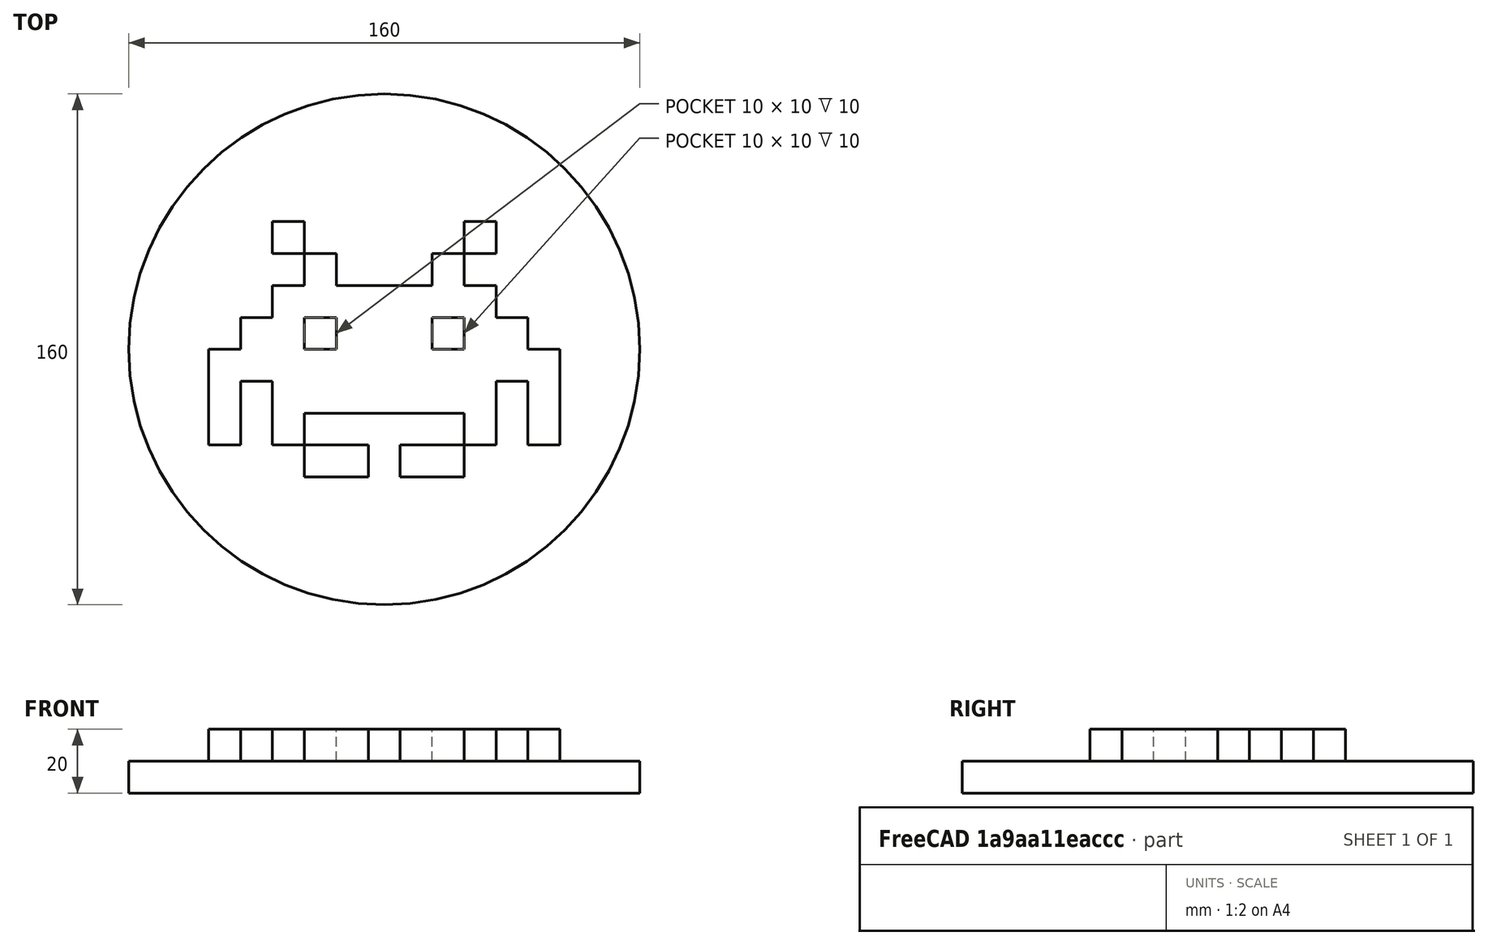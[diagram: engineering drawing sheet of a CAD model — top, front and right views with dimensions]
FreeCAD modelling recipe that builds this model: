
FCSTD DOCUMENT  (FreeCAD 0.17R13217 (Git))
Label: 02-1-moneda-space-invaders
License: All rights reserved
LicenseURL: http://en.wikipedia.org/wiki/All_rights_reserved
objects: Part::Box×18, Part::MultiFuse×2, Part::Cylinder×1
note: 21 computed .brp shape members not serialized (recipe doc carries the construction recipe); baked Part::Feature solids carry a one-line shape summary decoded from their .brp

FEATURE [Part::Box] Box  label="Cubo"
  AttacherType = Attacher::AttachEngine3D
  Height = 10
  Length = 10
  Width = 10
FEATURE [Part::Box] Box001  label="Cubo001"
  AttacherType = Attacher::AttachEngine3D
  Height = 10
  Length = 10
  Placement = pos=(10,-10,0) rot=(0,0,1;0rad)
  Width = 10
FEATURE [Part::Box] Box002  label="Cubo002"
  AttacherType = Attacher::AttachEngine3D
  Height = 10
  Length = 70
  Placement = pos=(0,-20,0) rot=(0,0,1;0rad)
  Width = 10
FEATURE [Part::Box] Box003  label="Cubo003"
  AttacherType = Attacher::AttachEngine3D
  Height = 10
  Length = 20
  Placement = pos=(-10,-30,0) rot=(0,0,1;0rad)
  Width = 10
FEATURE [Part::Box] Box004  label="Cubo004"
  AttacherType = Attacher::AttachEngine3D
  Height = 10
  Length = 10
  Placement = pos=(60,0,0) rot=(0,0,1;0rad)
  Width = 10
FEATURE [Part::Box] Box005  label="Cubo005"
  AttacherType = Attacher::AttachEngine3D
  Height = 10
  Length = 10
  Placement = pos=(50,-10,0) rot=(0,0,1;0rad)
  Width = 10
FEATURE [Part::Box] Box006  label="Cubo006"
  AttacherType = Attacher::AttachEngine3D
  Height = 10
  Length = 30
  Placement = pos=(20,-30,0) rot=(0,0,1;0rad)
  Width = 10
FEATURE [Part::Box] Box007  label="Cubo007"
  AttacherType = Attacher::AttachEngine3D
  Height = 10
  Length = 20
  Placement = pos=(60,-30,0) rot=(0,0,1;0rad)
  Width = 10
FEATURE [Part::Box] Box008  label="Cubo008"
  AttacherType = Attacher::AttachEngine3D
  Height = 10
  Length = 110
  Placement = pos=(-20,-40,0) rot=(0,0,1;0rad)
  Width = 10
FEATURE [Part::Box] Box009  label="Cubo009"
  AttacherType = Attacher::AttachEngine3D
  Height = 10
  Length = 10
  Placement = pos=(-20,-50,0) rot=(0,0,1;0rad)
  Width = 10
FEATURE [Part::Box] Box010  label="Cubo010"
  AttacherType = Attacher::AttachEngine3D
  Height = 10
  Length = 70
  Placement = pos=(0,-50,0) rot=(0,0,1;0rad)
  Width = 10
FEATURE [Part::Box] Box011  label="Cubo011"
  AttacherType = Attacher::AttachEngine3D
  Height = 10
  Length = 10
  Placement = pos=(80,-50,0) rot=(0,0,1;0rad)
  Width = 10
FEATURE [Part::Box] Box012  label="Cubo012"
  AttacherType = Attacher::AttachEngine3D
  Height = 10
  Length = 10
  Placement = pos=(-20,-60,0) rot=(0,0,1;0rad)
  Width = 10
FEATURE [Part::Box] Box013  label="Cubo013"
  AttacherType = Attacher::AttachEngine3D
  Height = 10
  Length = 10
  Placement = pos=(0,-60,0) rot=(0,0,1;0rad)
  Width = 10
FEATURE [Part::Box] Box014  label="Cubo014"
  AttacherType = Attacher::AttachEngine3D
  Height = 10
  Length = 10
  Placement = pos=(60,-60,0) rot=(0,0,1;0rad)
  Width = 10
FEATURE [Part::Box] Box015  label="Cubo015"
  AttacherType = Attacher::AttachEngine3D
  Height = 10
  Length = 10
  Placement = pos=(80,-60,0) rot=(0,0,1;0rad)
  Width = 10
FEATURE [Part::Box] Box016  label="Cubo016"
  AttacherType = Attacher::AttachEngine3D
  Height = 10
  Length = 20
  Placement = pos=(10,-70,0) rot=(0,0,1;0rad)
  Width = 10
FEATURE [Part::Box] Box017  label="Cubo017"
  AttacherType = Attacher::AttachEngine3D
  Height = 10
  Length = 20
  Placement = pos=(40,-70,0) rot=(0,0,1;0rad)
  Width = 10
FEATURE [Part::MultiFuse] Fusion
  Placement = pos=(-35,30,0) rot=(0,0,1;0rad)
  Refine = true
  Shapes = -> [Box,Box005,Box003,Box010,Box017,Box001,Box008,Box009,Box011,Box016,Box006,Box013,Box015,Box007,Box012,Box002,Box014,Box004]
FEATURE [Part::Cylinder] Cylinder  label="Cilindro"
  Angle = 360
  AttacherType = Attacher::AttachEngine3D
  Height = 10
  Placement = pos=(0,0,-10) rot=(0,0,1;0rad)
  Radius = 80
FEATURE [Part::MultiFuse] Fusion001
  Refine = true
  Shapes = -> [Fusion,Cylinder]
